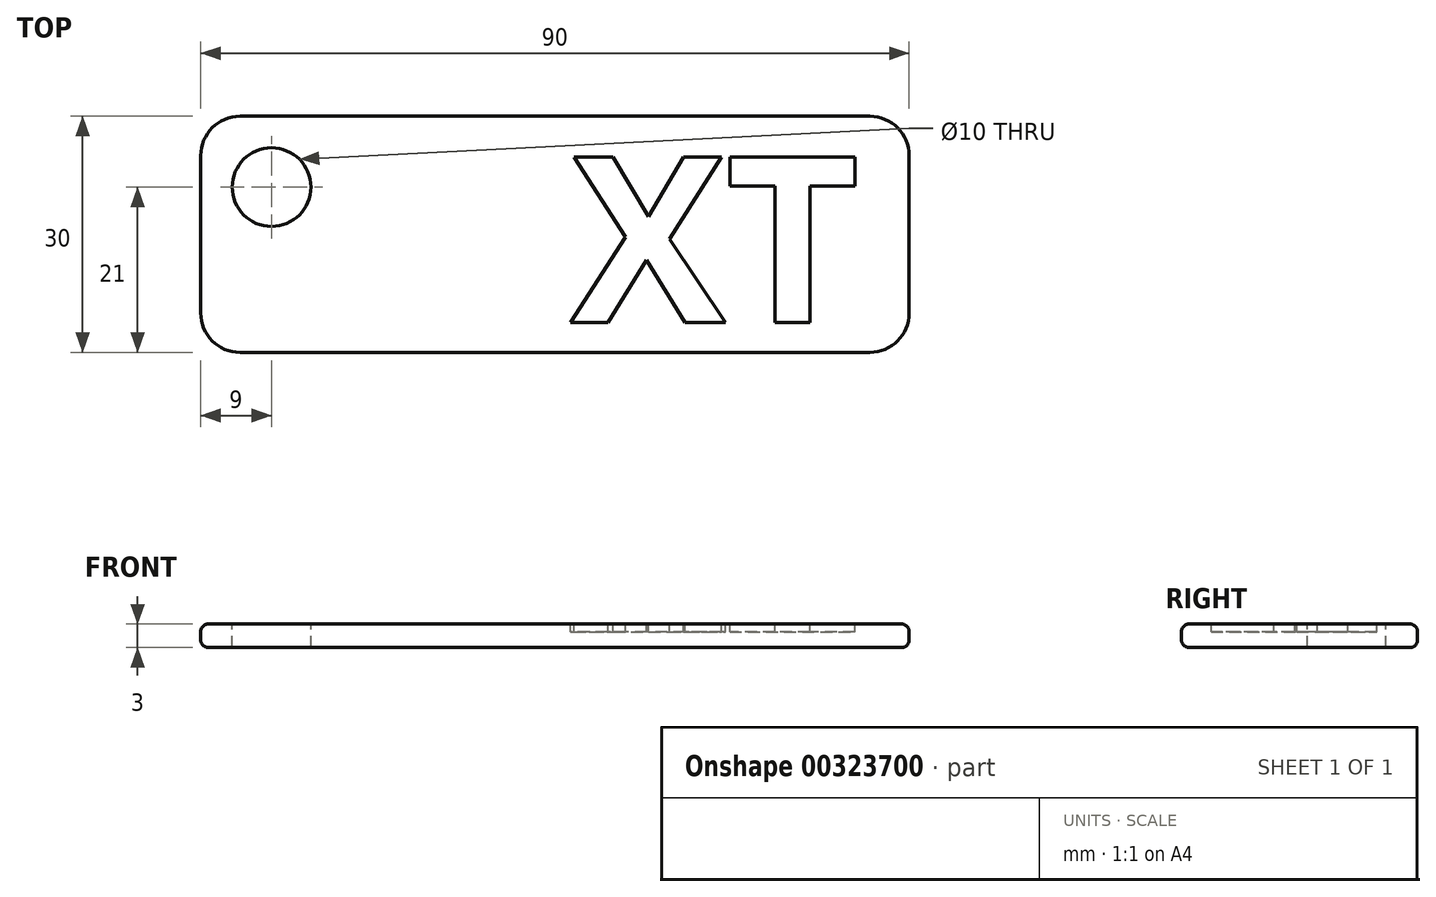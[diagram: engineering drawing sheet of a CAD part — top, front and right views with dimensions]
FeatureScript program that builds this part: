
annotation { "Feature Type Name" : "Feature", "Feature Type Description" : "" }
export const myFeature = defineFeature(function(context is Context, id is Id, definition is map)
    precondition{}
    {
        {
            var Q0;
            Q0=qCreatedBy(makeId("Top.planeOp"),FACE);
            var sketch = newSketch(context, id + "F0", { "sketchPlane" : qUnion([Q0])});
            skLineSegment(sketch, "E0.bottom", {"start": v(-45, 15) * mm, "end": v(45, 15) * mm});
            skLineSegment(sketch, "E0.top", {"start": v(-45, -15) * mm, "end": v(45, -15) * mm});
            skLineSegment(sketch, "E0.left", {"start": v(-45, 15) * mm, "end": v(-45, -15) * mm});
            skLineSegment(sketch, "E0.right", {"start": v(45, 15) * mm, "end": v(45, -15) * mm});
            skLineSegment(sketch, "E1", {"start": v(-45, 15) * mm, "end": v(45, -15) * mm, "construction": true});
            skSolve(sketch);
        }
        {
            var Q0;
            Q0=makeQuery(id+"F0.imprint","IMPRINT",FACE,{"disambiguationData":[TD([[makeQuery(id+"F0.imprint","IMPRINT",EDGE,{"derivedFrom":sQuery(id+"F0.wireOp",EDGE,"E0.bottom")}),-1.0]])]});
            extrude(context, id + "F1", {"entities" : qUnion([Q0]), "depth" : 3 * mm});
        }
        {
            var Q0;
            Q0=makeQuery(id+"F1.opExtrude","CAP_FACE",FACE,{"disambiguationData":[OSD([sQuery(id+"F0.wireOp",EDGE,"E0.bottom"),sQuery(id+"F0.wireOp",EDGE,"E0.top"),sQuery(id+"F0.wireOp",EDGE,"E0.left"),sQuery(id+"F0.wireOp",EDGE,"E0.right")])],"isStart":false});
            var Q1;
            Q1=makeQuery(id+"F1.opExtrude","CAP_FACE",FACE,{"disambiguationData":[OSD([sQuery(id+"F0.wireOp",EDGE,"E0.bottom"),sQuery(id+"F0.wireOp",EDGE,"E0.top"),sQuery(id+"F0.wireOp",EDGE,"E0.left"),sQuery(id+"F0.wireOp",EDGE,"E0.right")])],"isStart":true});
            fillet(context, id + "F2", {"entities" : qUnion([Q0, Q1]), "radius" : 1 * mm, "tangentPropagation" : true, "allowEdgeOverflow" : false});
        }
        {
            var Q0;
            Q0=makeQuery(id+"F1.opExtrude","SWEPT_EDGE",EDGE,{"disambiguationData":[OSD([sQuery(id+"F0.wireOp",EDGE,"E0.top"),sQuery(id+"F0.wireOp",EDGE,"E0.right")])]});
            var Q1;
            Q1=makeQuery(id+"F1.opExtrude","SWEPT_EDGE",EDGE,{"disambiguationData":[OSD([sQuery(id+"F0.wireOp",EDGE,"E0.bottom"),sQuery(id+"F0.wireOp",EDGE,"E0.right")])]});
            var Q2;
            Q2=makeQuery(id+"F1.opExtrude","SWEPT_EDGE",EDGE,{"disambiguationData":[OSD([sQuery(id+"F0.wireOp",EDGE,"E0.bottom"),sQuery(id+"F0.wireOp",EDGE,"E0.left")])]});
            var Q3;
            Q3=makeQuery(id+"F1.opExtrude","SWEPT_EDGE",EDGE,{"disambiguationData":[OSD([sQuery(id+"F0.wireOp",EDGE,"E0.top"),sQuery(id+"F0.wireOp",EDGE,"E0.left")])]});
            fillet(context, id + "F3", {"entities" : qUnion([Q0, Q1, Q2, Q3]), "radius" : 5 * mm, "tangentPropagation" : true, "allowEdgeOverflow" : false});
        }
        {
            var Q0;
            {var subQ0=sQuery(id+"F0.wireOp",EDGE,"E0.left");var subQ2=sQuery(id+"F0.wireOp",EDGE,"E0.bottom");var subQ4=sQuery(id+"F0.wireOp",EDGE,"E0.right");var subQ6=sQuery(id+"F0.wireOp",EDGE,"E0.top");Q0=makeQuery(id+"FmQCBBX3Ub0qneL_1.boolean.opBoolean","SPLIT",FACE,{"disambiguationData":[TD([makeQuery(id+"FmQCBBX3Ub0qneL_1.opExtrude","SWEPT_FACE",FACE,{"disambiguationData":[OSD([sQuery(id+"FOCoeRmDbjhRCuz_1.wireOp",EDGE,"4a1fb44a-e7be-4e23-9449-000d953c446c.sketch_text.stroke-0")])]})])],"derivedFrom":makeQuery(id+"F1.opExtrude","CAP_FACE",FACE,{"disambiguationData":[OSD([subQ2,subQ6,subQ0,subQ4])],"isStart":false})});}
            var sketch = newSketch(context, id + "F4", { "sketchPlane" : qUnion([Q0])});
            skCircle(sketch, "E2", {"center": v(-36, 6) * mm, "radius": 5 * mm});
            skSolve(sketch);
        }
        {
            var Q0;
            Q0=qSketchRegion(id+"F4",true);
            extrude(context, id + "F5", {"entities" : qUnion([Q0]), "operationType" : NewBodyOperationType.REMOVE, "oppositeDirection" : true, "depth" : 3 * mm});
        }
        {
            var Q0;
            Q0=makeQuery(id+"F1.opExtrude","CAP_FACE",FACE,{"disambiguationData":[OSD([sQuery(id+"F0.wireOp",EDGE,"E0.bottom"),sQuery(id+"F0.wireOp",EDGE,"E0.top"),sQuery(id+"F0.wireOp",EDGE,"E0.left"),sQuery(id+"F0.wireOp",EDGE,"E0.right")])],"isStart":false});
            var sketch = newSketch(context, id + "F6", { "sketchPlane" : qUnion([Q0])});
            skText(sketch, "E3", { "text": "XT", "fontName": "OpenSans-Bold.ttf"});
            const initialGuessF6  = {"E3": [0.002, -0.0112, 1, 0, 0.0212]};
            skSetInitialGuess(sketch, initialGuessF6);
            skSolve(sketch);
        }
        {
            var Q0;
            Q0=qSketchRegion(id+"F6",true);
            extrude(context, id + "F7", {"entities" : qUnion([Q0]), "operationType" : NewBodyOperationType.REMOVE, "oppositeDirection" : true, "depth" : 1 * mm});
        }
    });
